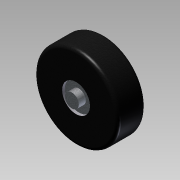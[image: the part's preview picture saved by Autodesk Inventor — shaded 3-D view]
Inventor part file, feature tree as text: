
AUTODESK INVENTOR PART (.ipt)
format: ipt  version: 2012 (Build 160160000, 160)  size: 130,560 bytes
history: native  units: in
note: dims shown in document units (in); Inventor stores cm internally (conversion verified against a paired STEP export)
features: extrude x5, sketch x5, fillet x1
ambient origin geometry x8: Origin, YZ Plane, XZ Plane, XY Plane, X Axis, Y Axis, Z Axis, Center Point
bodies: Solid1 (feature_tree)
feature tree (11):
  extrude  "Extrusion1"  Depth=1.0in TaperAngle=0.0deg
  extrude  "Extrusion2"  Depth=0.1in TaperAngle=0.0deg
  extrude  "Extrusion3"  Depth=0.1in TaperAngle=0.0deg
  fillet  "Fillet1"  Radius=0.125in
  extrude  "Extrusion4"  Depth=0.25in TaperAngle=0.0deg
  extrude  "Extrusion5"  Depth=0.25in TaperAngle=0.0deg
  sketch  "Sketch1"  dims[d0=3.0in d1=1.0in d2=0.0in]
  sketch  "Sketch2"  dims[d3=1.0in d4=0.1in d5=0.0in]
  sketch  "Sketch3"  dims[d6=1.0in d7=0.1in d8=0.0in d9=0.125in]
  sketch  "Sketch4"  dims[d10=0.5in d11=0.25in d12=0.0in]
  sketch  "Sketch5"  dims[d13=0.5in d14=0.25in d15=0.0in]
